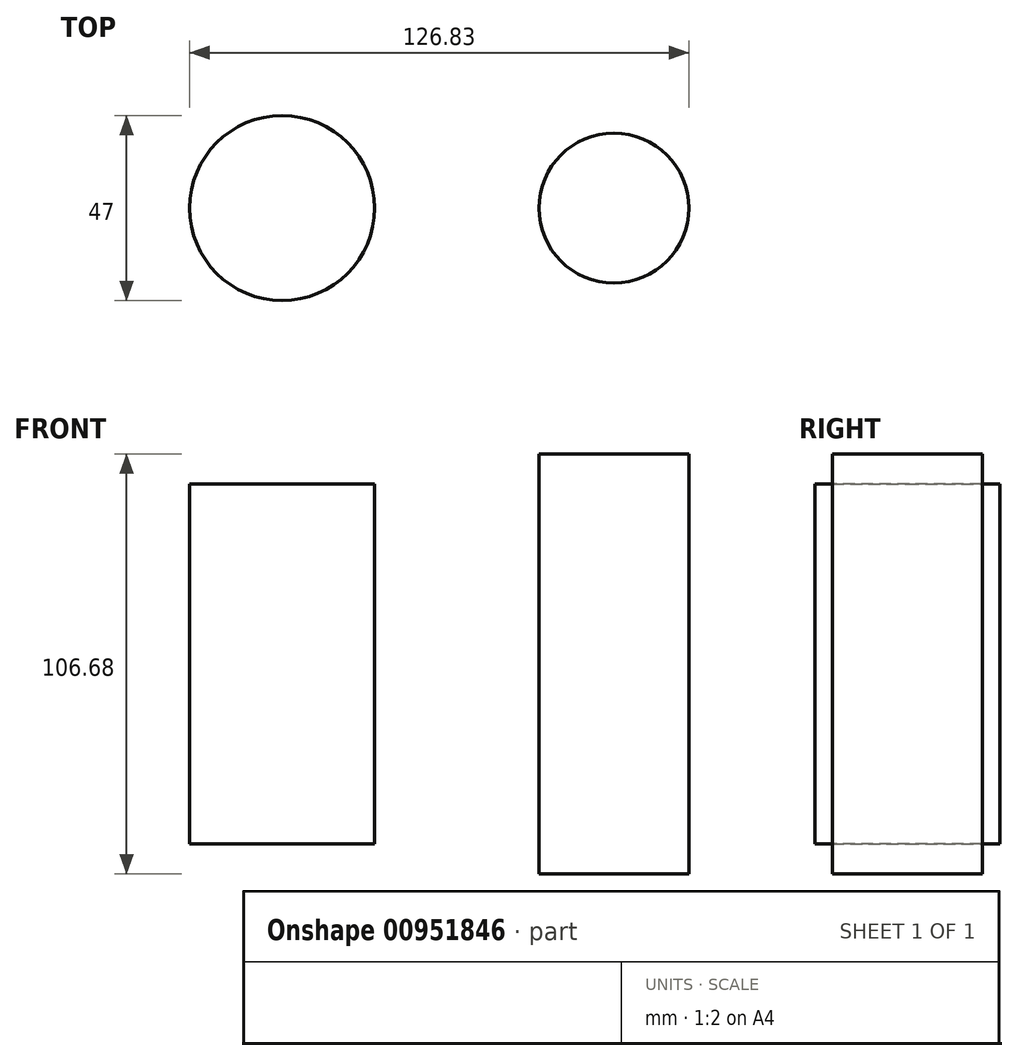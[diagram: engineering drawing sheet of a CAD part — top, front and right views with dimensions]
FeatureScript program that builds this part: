
annotation { "Feature Type Name" : "Feature", "Feature Type Description" : "" }
export const myFeature = defineFeature(function(context is Context, id is Id, definition is map)
    precondition{}
    {
        {
            var Q0;
            Q0=qCreatedBy(makeId("Top.planeOp"),FACE);
            var sketch = newSketch(context, id + "F0", { "sketchPlane" : qUnion([Q0])});
            skCircle(sketch, "E0", {"center": v(0, 0) * mm, "radius": 19.05 * mm});
            skSolve(sketch);
        }
        {
            var Q0;
            Q0=makeQuery(id+"F0.imprint","IMPRINT",FACE,{"disambiguationData":[TD([[makeQuery(id+"F0.imprint","IMPRINT",EDGE,{"derivedFrom":sQuery(id+"F0.wireOp",EDGE,"E0")}),1.0]])]});
            extrude(context, id + "F1", {"entities" : qUnion([Q0]), "endBound" : BoundingType.SYMMETRIC, "depth" : 106.68 * mm, "offsetDistance" : 25.4 * mm});
        }
        {
            var Q0;
            Q0=qCreatedBy(makeId("Top.planeOp"),FACE);
            var sketch = newSketch(context, id + "F2", { "sketchPlane" : qUnion([Q0])});
            skCircle(sketch, "E1", {"center": v(-84.29, 0) * mm, "radius": 23.5 * mm});
            skSolve(sketch);
        }
        {
            var Q0;
            Q0=makeQuery(id+"F2.imprint","IMPRINT",FACE,{"disambiguationData":[TD([[makeQuery(id+"F2.imprint","IMPRINT",EDGE,{"derivedFrom":sQuery(id+"F2.wireOp",EDGE,"E1")}),1.0]])]});
            extrude(context, id + "F3", {"entities" : qUnion([Q0]), "endBound" : BoundingType.SYMMETRIC, "depth" : 91.44 * mm, "offsetDistance" : 25.4 * mm});
        }
    });
